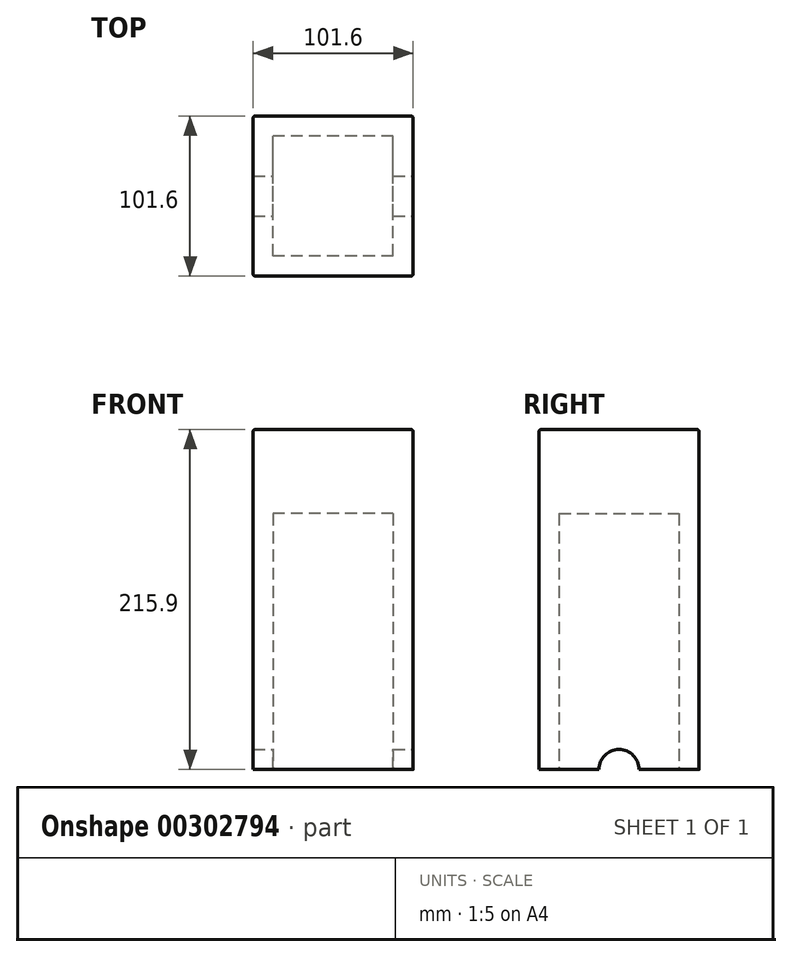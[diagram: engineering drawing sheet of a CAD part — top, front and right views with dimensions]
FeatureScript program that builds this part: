
annotation { "Feature Type Name" : "Feature", "Feature Type Description" : "" }
export const myFeature = defineFeature(function(context is Context, id is Id, definition is map)
    precondition{}
    {
        {
            var Q0;
            Q0=qCreatedBy(makeId("Top.planeOp"),FACE);
            var sketch = newSketch(context, id + "F0", { "sketchPlane" : qUnion([Q0])});
            skLineSegment(sketch, "E0.bottom", {"start": v(50.8, 50.8) * mm, "end": v(-50.8, 50.8) * mm});
            skLineSegment(sketch, "E0.top", {"start": v(50.8, -50.8) * mm, "end": v(-50.8, -50.8) * mm});
            skLineSegment(sketch, "E0.left", {"start": v(50.8, 50.8) * mm, "end": v(50.8, -50.8) * mm});
            skLineSegment(sketch, "E0.right", {"start": v(-50.8, 50.8) * mm, "end": v(-50.8, -50.8) * mm});
            skPoint(sketch, "E0.middle", {"position": v(0, 0) * mm});
            skSolve(sketch);
        }
        {
            var Q0;
            Q0=qSketchRegion(id+"F0",true);
            extrude(context, id + "F1", {"entities" : qUnion([Q0]), "depth" : 215.9 * mm});
        }
        {
            var Q0;
            Q0=makeQuery(id+"F1.opExtrude","CAP_FACE",FACE,{"disambiguationData":[OSD([sQuery(id+"F0.wireOp",EDGE,"E0.bottom"),sQuery(id+"F0.wireOp",EDGE,"E0.top"),sQuery(id+"F0.wireOp",EDGE,"E0.left"),sQuery(id+"F0.wireOp",EDGE,"E0.right")])],"isStart":true});
            var sketch = newSketch(context, id + "F2", { "sketchPlane" : qUnion([Q0])});
            skLineSegment(sketch, "E1.bottom", {"start": v(38.1, 38.1) * mm, "end": v(-38.1, 38.1) * mm});
            skLineSegment(sketch, "E1.top", {"start": v(38.1, -38.1) * mm, "end": v(-38.1, -38.1) * mm});
            skLineSegment(sketch, "E1.left", {"start": v(38.1, 38.1) * mm, "end": v(38.1, -38.1) * mm});
            skLineSegment(sketch, "E1.right", {"start": v(-38.1, 38.1) * mm, "end": v(-38.1, -38.1) * mm});
            skPoint(sketch, "E1.middle", {"position": v(0, 0) * mm});
            skSolve(sketch);
        }
        {
            var Q0;
            Q0=qSketchRegion(id+"F2",true);
            extrude(context, id + "F3", {"entities" : qUnion([Q0]), "operationType" : NewBodyOperationType.REMOVE, "oppositeDirection" : true, "depth" : 162.56 * mm});
        }
        {
            var Q0;
            Q0=makeQuery(id+"F1.opExtrude","SWEPT_EDGE",EDGE,{"disambiguationData":[OSD([sQuery(id+"F0.wireOp",EDGE,"E0.top"),sQuery(id+"F0.wireOp",EDGE,"E0.left")])]});
            var Q1;
            Q1=makeQuery(id+"F1.opExtrude","CAP_EDGE",EDGE,{"disambiguationData":[OSD([sQuery(id+"F0.wireOp",EDGE,"E0.left")])],"isStart":false});
            var Q2;
            Q2=makeQuery(id+"F1.opExtrude","SWEPT_EDGE",EDGE,{"disambiguationData":[OSD([sQuery(id+"F0.wireOp",EDGE,"E0.bottom"),sQuery(id+"F0.wireOp",EDGE,"E0.left")])]});
            var Q3;
            Q3=makeQuery(id+"F1.opExtrude","SWEPT_EDGE",EDGE,{"disambiguationData":[OSD([sQuery(id+"F0.wireOp",EDGE,"E0.top"),sQuery(id+"F0.wireOp",EDGE,"E0.right")])]});
            var Q4;
            Q4=makeQuery(id+"F1.opExtrude","CAP_EDGE",EDGE,{"disambiguationData":[OSD([sQuery(id+"F0.wireOp",EDGE,"E0.top")])],"isStart":false});
            var Q5;
            Q5=makeQuery(id+"F1.opExtrude","CAP_EDGE",EDGE,{"disambiguationData":[OSD([sQuery(id+"F0.wireOp",EDGE,"E0.bottom")])],"isStart":false});
            var Q6;
            Q6=makeQuery(id+"F1.opExtrude","SWEPT_EDGE",EDGE,{"disambiguationData":[OSD([sQuery(id+"F0.wireOp",EDGE,"E0.bottom"),sQuery(id+"F0.wireOp",EDGE,"E0.right")])]});
            var Q7;
            Q7=makeQuery(id+"F1.opExtrude","CAP_EDGE",EDGE,{"disambiguationData":[OSD([sQuery(id+"F0.wireOp",EDGE,"E0.right")])],"isStart":false});
            fillet(context, id + "F4", {"entities" : qUnion([Q0, Q1, Q2, Q3, Q4, Q5, Q6, Q7]), "radius" : 1.27 * mm, "tangentPropagation" : true, "allowEdgeOverflow" : false});
        }
        {
            var Q0;
            Q0=makeQuery(id+"F1.opExtrude","SWEPT_FACE",FACE,{"disambiguationData":[OSD([sQuery(id+"F0.wireOp",EDGE,"E0.left")])]});
            var sketch = newSketch(context, id + "F5", { "sketchPlane" : qUnion([Q0])});
            skCircle(sketch, "E2", {"center": v(0, 0) * mm, "radius": 12.7 * mm});
            skSolve(sketch);
        }
        {
            var Q0;
            Q0 = qSketchRegion(id + "F5", true);
            extrude(context, id + "F6", {"entities" : qUnion([Q0]), "operationType" : NewBodyOperationType.REMOVE, "endBound" : BoundingType.THROUGH_ALL, "oppositeDirection" : true, "depth" : 25.4 * mm});
        }
    });
